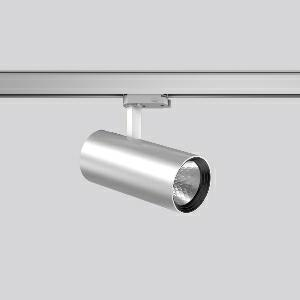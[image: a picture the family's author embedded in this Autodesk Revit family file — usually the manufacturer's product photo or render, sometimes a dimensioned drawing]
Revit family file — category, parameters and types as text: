
# Revit family: deecos_s_mini_742195_004_3_f840
name_source: partatom
category: Lighting Fixtures
units: mm (PartAtom-declared; Revit-internal decimal feet)

## family parameters
Cut with Voids When Loaded = No
Host = Face
Light Source = No
Part Type = Normal
Room Calculation Point = No
Round Connector Dimension = Use Diameter
Shared = No

## types (1)
- DEECOS S mini (1 x LED Modul 935, 2600 lm, 3500)
    Apparent Load = 20 VA
    Approval mark = CE
    CIE Flux Codes = 100 100 100 100 100
    Color Rendering = 92
    Color Temperature = 3500
    Default Elevation = 1800 mm
    Description = Series: DEECOS S mini
LED surface-mounted projector in modern design with no visible cooling ribs. Housing: die-cast aluminium, powder-coated. Rotation range: 356°. Swivel range: 90°. Black plastic ring and recessed LED to prevent glare from the side. Optical assembly with reflector made of MIRO-Silver with 98% total light reflection for outstanding efficiency - can be changed without tools. Best colour rendering index Ra>90. With multi adaptor for 3-circuit tracks 230 V. Suitable for Track on ceiling, Wall track. High quality converter without flickering and stroboscopic effect. The following accessories can be mounted without use of tools: interchangeable lenses, decorative glasses, honeycomb louvre, clear and frosted diffusers, white interchangeable plastic ring. 
Colour: silver
Diameter: 87 mm
Height: 214 mm
Lamp: LED
Socket: without socket
Colour temperature: 3500K
Colour rendering index (CRI): 92
System power: 20 W
Rated luminous flux: 2600 lm
Luminous efficiency: 130 lm/W
Control gear: Regulated power supply
Protection class: I
Type of protection: IP 20
    Height = 214 mm
    Lamp = 1 x LED Modul 935
    Lamp Light Flux = 2600 lm
    Lamp count = 1
    Length = 87 mm
    Lifetime = 50000 h
    Luminous efficacy = 130 lm/W
    Manufacturer = RZB
    ModVariant = No
    Model = 742195.004.3
    Mounting Place = Ceiling
    Mounting Type = Rail mounted
    Number of Poles = 1
    OnlyDefault = Yes
    Power Factor = 1
    Product Name = DEECOS S mini
    Product group = Track mounted projectors
    ProductGroupID = 301
    Protection Class = Protection class I
    Protection Degree = IP 20
    RLX_Detail_Level = 1
    RLX_Emergency_Light_Flux = 0 lm
    RLX_Emergency_Type = 0
    RLX_Emergency_Type_DB = No
    RlxData = <blob elided: 37113 chars, md5=f1c5087c>
    Socket = socket
    Standby Power = 0 W
    System Light Flux = 2600 lm
    System Power = 20 W
    Type Comments = Product without accessories
    Type Image = 741926.004.jpg
    URL = http://relux.com
    VarID = ---
    Voltage = 230 V
    Voltage Range = 220-240 V
    Weight = 0.00 kg
    Width = 0 mm  [stored 0 ft]

note: [stored X ft] marks values corroborated as IEEE doubles in the binary element streams (Revit-internal decimal feet)

## geometry (parser evidence)
native form markers: Blend x4, Sweep x13
no freeform markers — native parametric forms only
